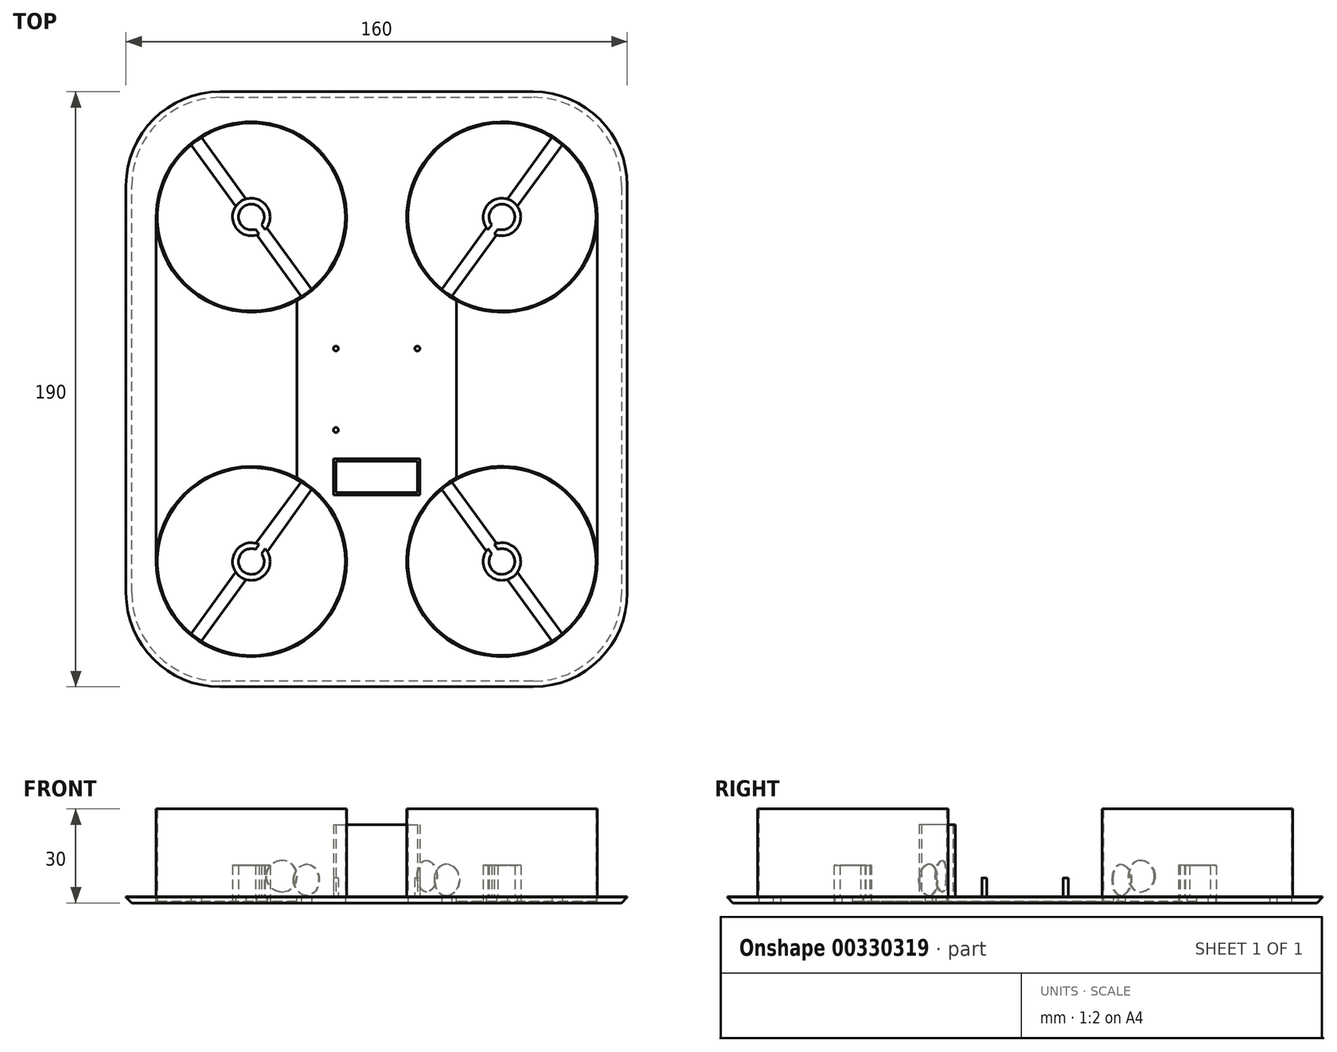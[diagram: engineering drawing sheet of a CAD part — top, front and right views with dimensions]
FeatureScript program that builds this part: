
annotation { "Feature Type Name" : "Feature", "Feature Type Description" : "" }
export const myFeature = defineFeature(function(context is Context, id is Id, definition is map)
    precondition{}
    {
        {
            var Q0;
            Q0=qCreatedBy(makeId("Top.planeOp"),FACE);
            var sketch = newSketch(context, id + "F0", { "sketchPlane" : qUnion([Q0])});
            skLineSegment(sketch, "E0.bottom", {"start": v(-80, 95) * mm, "end": v(80, 95) * mm});
            skLineSegment(sketch, "E0.top", {"start": v(-80, -95) * mm, "end": v(80, -95) * mm});
            skLineSegment(sketch, "E0.left", {"start": v(-80, 95) * mm, "end": v(-80, -95) * mm});
            skLineSegment(sketch, "E0.right", {"start": v(80, 95) * mm, "end": v(80, -95) * mm});
            skArc(sketch, "E1", {"start": v(-20.78, 31.97) * mm, "mid": v(-15.74, 72.65) * mm, "end": v(-55.99, 80.38) * mm});
            skLineSegment(sketch, "E2", {"start": v(-40, 132.2) * mm, "end": v(-40, -105.6) * mm, "construction": true});
            skLineSegment(sketch, "E3", {"start": v(-91.22, 55) * mm, "end": v(115.84, 55) * mm, "construction": true});
            skArc(sketch, "E4", {"start": v(55.99, 80.38) * mm, "mid": v(15.74, 72.65) * mm, "end": v(20.78, 31.97) * mm});
            skLineSegment(sketch, "E5", {"start": v(40, 97.12) * mm, "end": v(40, -118.42) * mm, "construction": true});
            skLineSegment(sketch, "E6", {"start": v(-111.72, -55) * mm, "end": v(120.79, -55) * mm, "construction": true});
            skArc(sketch, "E7", {"start": v(-55.99, -80.38) * mm, "mid": v(-15.74, -72.65) * mm, "end": v(-20.78, -31.97) * mm});
            skArc(sketch, "E8", {"start": v(20.78, -31.97) * mm, "mid": v(15.74, -72.65) * mm, "end": v(55.99, -80.38) * mm});
            skLineSegment(sketch, "E9", {"start": v(99.43, 136.72) * mm, "end": v(-85.41, -117.45) * mm, "construction": true});
            skLineSegment(sketch, "E10", {"start": v(-83.26, 114.48) * mm, "end": v(79.72, -109.61) * mm, "construction": true});
            skLineSegment(sketch, "E11", {"start": v(-55.99, 80.38) * mm, "end": v(-41.7, 60.75) * mm});
            skLineSegment(sketch, "E12", {"start": v(-59.22, 78.03) * mm, "end": v(-44.94, 58.4) * mm});
            skArc(sketch, "E13.trimOffspring", {"start": v(-59.22, 78.03) * mm, "mid": v(-64.26, 37.35) * mm, "end": v(-24.01, 29.62) * mm});
            skLineSegment(sketch, "E14.MirrorCS", {"start": v(55.99, 80.38) * mm, "end": v(41.7, 60.75) * mm});
            skLineSegment(sketch, "E15.MirrorCS", {"start": v(59.22, 78.03) * mm, "end": v(44.94, 58.4) * mm});
            skLineSegment(sketch, "E16.MirrorCS", {"start": v(-59.22, -78.03) * mm, "end": v(-44.94, -58.4) * mm});
            skLineSegment(sketch, "E17.MirrorCS", {"start": v(-55.99, -80.38) * mm, "end": v(-41.7, -60.75) * mm});
            skLineSegment(sketch, "E18.MirrorCS", {"start": v(55.99, -80.38) * mm, "end": v(41.7, -60.75) * mm});
            skLineSegment(sketch, "E19.MirrorCS", {"start": v(59.22, -78.03) * mm, "end": v(44.94, -58.4) * mm});
            skArc(sketch, "E20.trimOffspring", {"start": v(24.01, 29.62) * mm, "mid": v(64.26, 37.35) * mm, "end": v(59.22, 78.03) * mm});
            skArc(sketch, "E21.trimOffspring", {"start": v(59.22, -78.03) * mm, "mid": v(64.26, -37.35) * mm, "end": v(24.01, -29.62) * mm});
            skArc(sketch, "E22.trimOffspring", {"start": v(-24.01, -29.62) * mm, "mid": v(-64.26, -37.35) * mm, "end": v(-59.22, -78.03) * mm});
            skArc(sketch, "E23", {"start": v(-35.06, 51.6) * mm, "mid": v(-35.15, 58.53) * mm, "end": v(-41.7, 60.75) * mm});
            skArc(sketch, "E24", {"start": v(41.7, 60.75) * mm, "mid": v(35.15, 58.53) * mm, "end": v(35.06, 51.6) * mm});
            skArc(sketch, "E25", {"start": v(-38.56, -49.18) * mm, "mid": v(-44.93, -51.58) * mm, "end": v(-44.94, -58.4) * mm});
            skArc(sketch, "E26", {"start": v(44.94, -58.4) * mm, "mid": v(44.85, -51.47) * mm, "end": v(38.3, -49.25) * mm});
            skLineSegment(sketch, "E27.trimOffspring", {"start": v(-35.06, 51.6) * mm, "end": v(-20.78, 31.97) * mm});
            skLineSegment(sketch, "E28.trimOffspring", {"start": v(-38.3, 49.25) * mm, "end": v(-24.01, 29.62) * mm});
            skArc(sketch, "E29.trimOffspring", {"start": v(-44.94, 58.4) * mm, "mid": v(-44.85, 51.47) * mm, "end": v(-38.3, 49.25) * mm});
            skLineSegment(sketch, "E30.trimOffspring", {"start": v(35.06, 51.6) * mm, "end": v(20.78, 31.97) * mm});
            skLineSegment(sketch, "E31.trimOffspring", {"start": v(38.3, 49.25) * mm, "end": v(24.01, 29.62) * mm});
            skArc(sketch, "E32.trimOffspring", {"start": v(38.3, 49.25) * mm, "mid": v(44.85, 51.47) * mm, "end": v(44.94, 58.4) * mm});
            skLineSegment(sketch, "E33.trimOffspring", {"start": v(-34.9, -51.83) * mm, "end": v(-20.78, -31.97) * mm});
            skLineSegment(sketch, "E34.trimOffspring", {"start": v(-38.56, -49.18) * mm, "end": v(-24.01, -29.62) * mm});
            skArc(sketch, "E35.trimOffspring", {"start": v(-41.7, -60.75) * mm, "mid": v(-35.23, -58.64) * mm, "end": v(-34.9, -51.83) * mm});
            skLineSegment(sketch, "E36.trimOffspring", {"start": v(38.3, -49.25) * mm, "end": v(24.01, -29.62) * mm});
            skLineSegment(sketch, "E37.trimOffspring", {"start": v(35.06, -51.6) * mm, "end": v(20.78, -31.97) * mm});
            skArc(sketch, "E38.trimOffspring", {"start": v(35.06, -51.6) * mm, "mid": v(35.15, -58.53) * mm, "end": v(41.7, -60.75) * mm});
            skSolve(sketch);
        }
        {
            var Q0;
            Q0 = qSketchRegion(id + "F0", true);
            extrude(context, id + "F1", {"entities" : qUnion([Q0]), "depth" : 2 * mm});
        }
        {
            var Q0;
            Q0=makeQuery(id+"F1.opExtrude","SWEPT_EDGE",EDGE,{"disambiguationData":[OSD([sQuery(id+"F0.wireOp",EDGE,"E0.bottom"),sQuery(id+"F0.wireOp",EDGE,"E0.left")])]});
            var Q1;
            Q1=makeQuery(id+"F1.opExtrude","SWEPT_EDGE",EDGE,{"disambiguationData":[OSD([sQuery(id+"F0.wireOp",EDGE,"E0.bottom"),sQuery(id+"F0.wireOp",EDGE,"E0.right")])]});
            var Q2;
            Q2=makeQuery(id+"F1.opExtrude","SWEPT_EDGE",EDGE,{"disambiguationData":[OSD([sQuery(id+"F0.wireOp",EDGE,"E0.top"),sQuery(id+"F0.wireOp",EDGE,"E0.right")])]});
            var Q3;
            Q3=makeQuery(id+"F1.opExtrude","SWEPT_EDGE",EDGE,{"disambiguationData":[OSD([sQuery(id+"F0.wireOp",EDGE,"E0.top"),sQuery(id+"F0.wireOp",EDGE,"E0.left")])]});
            fillet(context, id + "F2", {"entities" : qUnion([Q0, Q1, Q2, Q3]), "radius" : 30 * mm, "tangentPropagation" : true, "allowEdgeOverflow" : false});
        }
        {
            var Q0;
            Q0=qCreatedBy(makeId("Top.planeOp"),FACE);
            var sketch = newSketch(context, id + "F3", { "sketchPlane" : qUnion([Q0])});
            skArc(sketch, "E39", {"start": v(-35.57, 50.95) * mm, "mid": v(-43.53, 59.85) * mm, "end": v(-37.51, 49.54) * mm});
            skArc(sketch, "E40", {"start": v(-36.72, 52.54) * mm, "mid": v(-42.41, 58.32) * mm, "end": v(-38.66, 51.12) * mm});
            skLineSegment(sketch, "E41", {"start": v(-48.35, 66.48) * mm, "end": v(-31.44, 43.23) * mm, "construction": true});
            skLineSegment(sketch, "E42", {"start": v(-36.72, 52.54) * mm, "end": v(-35.57, 50.95) * mm});
            skLineSegment(sketch, "E43.MirrorCS", {"start": v(-38.66, 51.12) * mm, "end": v(-37.51, 49.54) * mm});
            skArc(sketch, "E44.MirrorCS", {"start": v(36.72, 52.54) * mm, "mid": v(42.41, 58.32) * mm, "end": v(38.66, 51.12) * mm});
            skArc(sketch, "E45.MirrorCS", {"start": v(35.57, 50.95) * mm, "mid": v(43.53, 59.85) * mm, "end": v(37.51, 49.54) * mm});
            skLineSegment(sketch, "E46.MirrorCS", {"start": v(36.72, 52.54) * mm, "end": v(35.57, 50.95) * mm});
            skLineSegment(sketch, "E47.MirrorCS", {"start": v(38.66, 51.12) * mm, "end": v(37.51, 49.54) * mm});
            skArc(sketch, "E48.MirrorCS", {"start": v(35.57, -50.95) * mm, "mid": v(43.53, -59.85) * mm, "end": v(37.51, -49.54) * mm});
            skArc(sketch, "E49.MirrorCS", {"start": v(36.72, -52.54) * mm, "mid": v(42.41, -58.32) * mm, "end": v(38.66, -51.12) * mm});
            skLineSegment(sketch, "E50.MirrorCS", {"start": v(38.66, -51.12) * mm, "end": v(37.51, -49.54) * mm});
            skLineSegment(sketch, "E51.MirrorCS", {"start": v(36.72, -52.54) * mm, "end": v(35.57, -50.95) * mm});
            skArc(sketch, "E52.MirrorCS", {"start": v(-36.72, -52.54) * mm, "mid": v(-42.41, -58.32) * mm, "end": v(-38.66, -51.12) * mm});
            skLineSegment(sketch, "E53.MirrorCS", {"start": v(-36.72, -52.54) * mm, "end": v(-35.57, -50.95) * mm});
            skLineSegment(sketch, "E54.MirrorCS", {"start": v(-38.66, -51.12) * mm, "end": v(-37.51, -49.54) * mm});
            skArc(sketch, "E55.MirrorCS", {"start": v(-35.57, -50.95) * mm, "mid": v(-43.53, -59.85) * mm, "end": v(-37.51, -49.54) * mm});
            skSolve(sketch);
        }
        {
            var Q0;
            Q0 = qSketchRegion(id + "F3", true);
            extrude(context, id + "F4", {"entities" : qUnion([Q0]), "operationType" : NewBodyOperationType.ADD, "depth" : 12 * mm});
        }
        {
            var Q0;
            Q0=qCreatedBy(makeId("Top.planeOp"),FACE);
            var sketch = newSketch(context, id + "F5", { "sketchPlane" : qUnion([Q0])});
            skCircle(sketch, "E56", {"center": v(-40, 55) * mm, "radius": 30 * mm});
            skCircle(sketch, "E57", {"center": v(-40, 55) * mm, "radius": 30.4 * mm});
            skCircle(sketch, "E58.MirrorC", {"center": v(40, 55) * mm, "radius": 30.4 * mm});
            skCircle(sketch, "E59.MirrorC", {"center": v(40, 55) * mm, "radius": 30 * mm});
            skCircle(sketch, "E60.MirrorC", {"center": v(-40, -55) * mm, "radius": 30.4 * mm});
            skCircle(sketch, "E61.MirrorC", {"center": v(-40, -55) * mm, "radius": 30 * mm});
            skCircle(sketch, "E62.MirrorC", {"center": v(40, -55) * mm, "radius": 30.4 * mm});
            skCircle(sketch, "E63.MirrorC", {"center": v(40, -55) * mm, "radius": 30 * mm});
            skSolve(sketch);
        }
        {
            var Q0;
            Q0 = qSketchRegion(id + "F5", true);
            extrude(context, id + "F6", {"entities" : qUnion([Q0]), "operationType" : NewBodyOperationType.ADD, "depth" : 30 * mm});
        }
        {
            var Q0;
            Q0=qCreatedBy(makeId("Front.planeOp"),FACE);
            var sketch = newSketch(context, id + "F7", { "sketchPlane" : qUnion([Q0])});
            skLineSegment(sketch, "E64", {"start": v(0, 70.13) * mm, "end": v(0, -36.6) * mm, "construction": true});
            skSolve(sketch);
        }
        {
            var Q0;
            Q0=sQuery(id+"F7.wireOp",EDGE,"E64");
            cPlane(context, id + "F8", {"entities" : qUnion([Q0]), "cplaneType" : CPlaneType.LINE_ANGLE, "offset" : 25 * mm, "angle" : 54 * degree, "width" : 150 * mm, "height" : 150 * mm});
        }
        {
            var Q0;
            Q0=qCreatedBy(id+"F8.planeOp",FACE);
            var sketch = newSketch(context, id + "F9", { "sketchPlane" : qUnion([Q0])});
            skCircle(sketch, "E65", {"center": v(0, 7.35) * mm, "radius": 5 * mm});
            skSolve(sketch);
        }
        {
            var Q0;
            Q0=makeQuery(id+"F9.imprint","IMPRINT",FACE,{"disambiguationData":[TD([[makeQuery(id+"F9.imprint","IMPRINT",EDGE,{"derivedFrom":sQuery(id+"F9.wireOp",EDGE,"E65")}),1.0]])]});
            extrude(context, id + "F10", {"entities" : qUnion([Q0]), "operationType" : NewBodyOperationType.REMOVE, "oppositeDirection" : true, "depth" : 60 * mm, "hasSecondDirection" : true, "secondDirectionOppositeDirection" : false, "secondDirectionDepth" : 60 * mm});
        }
        {
            var Q0;
            Q0=sQuery(id+"F7.wireOp",EDGE,"E64");
            cPlane(context, id + "F11", {"entities" : qUnion([Q0]), "cplaneType" : CPlaneType.LINE_ANGLE, "offset" : 25 * mm, "angle" : 126 * degree, "width" : 150 * mm, "height" : 150 * mm});
        }
        {
            var Q0;
            Q0=qCreatedBy(id+"F11.planeOp",FACE);
            var sketch = newSketch(context, id + "F12", { "sketchPlane" : qUnion([Q0])});
            skCircle(sketch, "E66", {"center": v(8.82, 8.55) * mm, "radius": 5 * mm});
            skSolve(sketch);
        }
        {
            var Q0;
            Q0=makeQuery(id+"F12.imprint","IMPRINT",FACE,{"disambiguationData":[TD([[makeQuery(id+"F12.imprint","IMPRINT",EDGE,{"derivedFrom":sQuery(id+"F12.wireOp",EDGE,"E66")}),1.0]])]});
            extrude(context, id + "F13", {"entities" : qUnion([Q0]), "operationType" : NewBodyOperationType.REMOVE, "oppositeDirection" : true, "depth" : 50 * mm, "hasSecondDirection" : true, "secondDirectionOppositeDirection" : false, "secondDirectionDepth" : 50 * mm});
        }
        {
            var Q0;
            Q0=qCreatedBy(makeId("Top.planeOp"),FACE);
            var sketch = newSketch(context, id + "F14", { "sketchPlane" : qUnion([Q0])});
            skCircle(sketch, "E67", {"center": v(-13, 13) * mm, "radius": 0.8 * mm});
            skCircle(sketch, "E68", {"center": v(13, 13) * mm, "radius": 0.8 * mm});
            skCircle(sketch, "E69", {"center": v(-13, -13) * mm, "radius": 0.8 * mm});
            skSolve(sketch);
        }
        {
            var Q0;
            Q0 = qSketchRegion(id + "F14", true);
            extrude(context, id + "F15", {"entities" : qUnion([Q0]), "operationType" : NewBodyOperationType.ADD, "depth" : 8 * mm});
        }
        {
            var Q0;
            Q0=qCreatedBy(makeId("Top.planeOp"),FACE);
            var sketch = newSketch(context, id + "F16", { "sketchPlane" : qUnion([Q0])});
            skLineSegment(sketch, "E70.bottom", {"start": v(-13, -23) * mm, "end": v(13, -23) * mm});
            skLineSegment(sketch, "E70.top", {"start": v(-13, -33) * mm, "end": v(13, -33) * mm});
            skLineSegment(sketch, "E70.left", {"start": v(-13, -23) * mm, "end": v(-13, -33) * mm});
            skLineSegment(sketch, "E70.right", {"start": v(13, -23) * mm, "end": v(13, -33) * mm});
            skLineSegment(sketch, "E71.0", {"start": v(-13.8, -22.2) * mm, "end": v(13.8, -22.2) * mm});
            skLineSegment(sketch, "E71.1", {"start": v(-13.8, -22.2) * mm, "end": v(-13.8, -33.8) * mm});
            skLineSegment(sketch, "E71.2", {"start": v(-13.8, -33.8) * mm, "end": v(13.8, -33.8) * mm});
            skLineSegment(sketch, "E71.3", {"start": v(13.8, -22.2) * mm, "end": v(13.8, -33.8) * mm});
            skSolve(sketch);
        }
        {
            var Q0;
            Q0 = qSketchRegion(id + "F16", true);
            extrude(context, id + "F17", {"entities" : qUnion([Q0]), "operationType" : NewBodyOperationType.ADD, "depth" : 25 * mm});
        }
        {
            var Q0;
            Q0=makeQuery(id+"F1.opExtrude","CAP_EDGE",EDGE,{"disambiguationData":[OSD([sQuery(id+"F0.wireOp",EDGE,"E0.right")])],"isStart":true});
            var Q1;
            {var subQ0=sQuery(id+"F0.wireOp",EDGE,"E0.right");var subQ1=sQuery(id+"F0.wireOp",EDGE,"E0.top");Q1=makeQuery(id+"F2.opFillet","BLEND_EDGE",EDGE,{"blendedFrom":[makeQuery(id+"F1.opExtrude","SWEPT_EDGE",EDGE,{"disambiguationData":[OSD([subQ1,subQ0])]}),makeQuery(id+"F1.opExtrude","CAP_FACE",FACE,{"disambiguationData":[OSD([sQuery(id+"F0.wireOp",EDGE,"E0.bottom"),subQ1,sQuery(id+"F0.wireOp",EDGE,"E0.left"),subQ0,sQuery(id+"F0.wireOp",EDGE,"E1"),sQuery(id+"F0.wireOp",EDGE,"E4"),sQuery(id+"F0.wireOp",EDGE,"E7"),sQuery(id+"F0.wireOp",EDGE,"E8"),sQuery(id+"F0.wireOp",EDGE,"E11"),sQuery(id+"F0.wireOp",EDGE,"E12"),sQuery(id+"F0.wireOp",EDGE,"E13.trimOffspring"),sQuery(id+"F0.wireOp",EDGE,"E14.MirrorCS"),sQuery(id+"F0.wireOp",EDGE,"E15.MirrorCS"),sQuery(id+"F0.wireOp",EDGE,"E16.MirrorCS"),sQuery(id+"F0.wireOp",EDGE,"E17.MirrorCS"),sQuery(id+"F0.wireOp",EDGE,"E18.MirrorCS"),sQuery(id+"F0.wireOp",EDGE,"E19.MirrorCS"),sQuery(id+"F0.wireOp",EDGE,"E20.trimOffspring"),sQuery(id+"F0.wireOp",EDGE,"E21.trimOffspring"),sQuery(id+"F0.wireOp",EDGE,"E22.trimOffspring"),sQuery(id+"F0.wireOp",EDGE,"E23"),sQuery(id+"F0.wireOp",EDGE,"E24"),sQuery(id+"F0.wireOp",EDGE,"E25"),sQuery(id+"F0.wireOp",EDGE,"E26"),sQuery(id+"F0.wireOp",EDGE,"E27.trimOffspring"),sQuery(id+"F0.wireOp",EDGE,"E28.trimOffspring"),sQuery(id+"F0.wireOp",EDGE,"E29.trimOffspring"),sQuery(id+"F0.wireOp",EDGE,"E30.trimOffspring"),sQuery(id+"F0.wireOp",EDGE,"E31.trimOffspring"),sQuery(id+"F0.wireOp",EDGE,"E32.trimOffspring"),sQuery(id+"F0.wireOp",EDGE,"E33.trimOffspring"),sQuery(id+"F0.wireOp",EDGE,"E34.trimOffspring"),sQuery(id+"F0.wireOp",EDGE,"E35.trimOffspring"),sQuery(id+"F0.wireOp",EDGE,"E37.trimOffspring"),sQuery(id+"F0.wireOp",EDGE,"E38.trimOffspring"),sQuery(id+"F0.wireOp",EDGE,"E36.trimOffspring")])],"isStart":true})],"blendedInto":[makeQuery(id+"F1.opExtrude","CAP_FACE",FACE,{"disambiguationData":[OSD([sQuery(id+"F0.wireOp",EDGE,"E0.bottom"),subQ1,sQuery(id+"F0.wireOp",EDGE,"E0.left"),subQ0,sQuery(id+"F0.wireOp",EDGE,"E1"),sQuery(id+"F0.wireOp",EDGE,"E4"),sQuery(id+"F0.wireOp",EDGE,"E7"),sQuery(id+"F0.wireOp",EDGE,"E8"),sQuery(id+"F0.wireOp",EDGE,"E11"),sQuery(id+"F0.wireOp",EDGE,"E12"),sQuery(id+"F0.wireOp",EDGE,"E13.trimOffspring"),sQuery(id+"F0.wireOp",EDGE,"E14.MirrorCS"),sQuery(id+"F0.wireOp",EDGE,"E15.MirrorCS"),sQuery(id+"F0.wireOp",EDGE,"E16.MirrorCS"),sQuery(id+"F0.wireOp",EDGE,"E17.MirrorCS"),sQuery(id+"F0.wireOp",EDGE,"E18.MirrorCS"),sQuery(id+"F0.wireOp",EDGE,"E19.MirrorCS"),sQuery(id+"F0.wireOp",EDGE,"E20.trimOffspring"),sQuery(id+"F0.wireOp",EDGE,"E21.trimOffspring"),sQuery(id+"F0.wireOp",EDGE,"E22.trimOffspring"),sQuery(id+"F0.wireOp",EDGE,"E23"),sQuery(id+"F0.wireOp",EDGE,"E24"),sQuery(id+"F0.wireOp",EDGE,"E25"),sQuery(id+"F0.wireOp",EDGE,"E26"),sQuery(id+"F0.wireOp",EDGE,"E27.trimOffspring"),sQuery(id+"F0.wireOp",EDGE,"E28.trimOffspring"),sQuery(id+"F0.wireOp",EDGE,"E29.trimOffspring"),sQuery(id+"F0.wireOp",EDGE,"E30.trimOffspring"),sQuery(id+"F0.wireOp",EDGE,"E31.trimOffspring"),sQuery(id+"F0.wireOp",EDGE,"E32.trimOffspring"),sQuery(id+"F0.wireOp",EDGE,"E33.trimOffspring"),sQuery(id+"F0.wireOp",EDGE,"E34.trimOffspring"),sQuery(id+"F0.wireOp",EDGE,"E35.trimOffspring"),sQuery(id+"F0.wireOp",EDGE,"E37.trimOffspring"),sQuery(id+"F0.wireOp",EDGE,"E38.trimOffspring"),sQuery(id+"F0.wireOp",EDGE,"E36.trimOffspring")])],"isStart":true})]});}
            var Q2;
            Q2=makeQuery(id+"F1.opExtrude","CAP_EDGE",EDGE,{"disambiguationData":[OSD([sQuery(id+"F0.wireOp",EDGE,"E0.top")])],"isStart":true});
            var Q3;
            {var subQ0=sQuery(id+"F0.wireOp",EDGE,"E0.left");var subQ1=sQuery(id+"F0.wireOp",EDGE,"E0.top");Q3=makeQuery(id+"F2.opFillet","BLEND_EDGE",EDGE,{"blendedFrom":[makeQuery(id+"F1.opExtrude","SWEPT_EDGE",EDGE,{"disambiguationData":[OSD([subQ1,subQ0])]}),makeQuery(id+"F1.opExtrude","CAP_FACE",FACE,{"disambiguationData":[OSD([sQuery(id+"F0.wireOp",EDGE,"E0.bottom"),subQ1,subQ0,sQuery(id+"F0.wireOp",EDGE,"E0.right"),sQuery(id+"F0.wireOp",EDGE,"E1"),sQuery(id+"F0.wireOp",EDGE,"E4"),sQuery(id+"F0.wireOp",EDGE,"E7"),sQuery(id+"F0.wireOp",EDGE,"E8"),sQuery(id+"F0.wireOp",EDGE,"E11"),sQuery(id+"F0.wireOp",EDGE,"E12"),sQuery(id+"F0.wireOp",EDGE,"E13.trimOffspring"),sQuery(id+"F0.wireOp",EDGE,"E14.MirrorCS"),sQuery(id+"F0.wireOp",EDGE,"E15.MirrorCS"),sQuery(id+"F0.wireOp",EDGE,"E16.MirrorCS"),sQuery(id+"F0.wireOp",EDGE,"E17.MirrorCS"),sQuery(id+"F0.wireOp",EDGE,"E18.MirrorCS"),sQuery(id+"F0.wireOp",EDGE,"E19.MirrorCS"),sQuery(id+"F0.wireOp",EDGE,"E20.trimOffspring"),sQuery(id+"F0.wireOp",EDGE,"E21.trimOffspring"),sQuery(id+"F0.wireOp",EDGE,"E22.trimOffspring"),sQuery(id+"F0.wireOp",EDGE,"E23"),sQuery(id+"F0.wireOp",EDGE,"E24"),sQuery(id+"F0.wireOp",EDGE,"E25"),sQuery(id+"F0.wireOp",EDGE,"E26"),sQuery(id+"F0.wireOp",EDGE,"E27.trimOffspring"),sQuery(id+"F0.wireOp",EDGE,"E28.trimOffspring"),sQuery(id+"F0.wireOp",EDGE,"E29.trimOffspring"),sQuery(id+"F0.wireOp",EDGE,"E30.trimOffspring"),sQuery(id+"F0.wireOp",EDGE,"E31.trimOffspring"),sQuery(id+"F0.wireOp",EDGE,"E32.trimOffspring"),sQuery(id+"F0.wireOp",EDGE,"E33.trimOffspring"),sQuery(id+"F0.wireOp",EDGE,"E34.trimOffspring"),sQuery(id+"F0.wireOp",EDGE,"E35.trimOffspring"),sQuery(id+"F0.wireOp",EDGE,"E37.trimOffspring"),sQuery(id+"F0.wireOp",EDGE,"E38.trimOffspring"),sQuery(id+"F0.wireOp",EDGE,"E36.trimOffspring")])],"isStart":true})],"blendedInto":[makeQuery(id+"F1.opExtrude","CAP_FACE",FACE,{"disambiguationData":[OSD([sQuery(id+"F0.wireOp",EDGE,"E0.bottom"),subQ1,subQ0,sQuery(id+"F0.wireOp",EDGE,"E0.right"),sQuery(id+"F0.wireOp",EDGE,"E1"),sQuery(id+"F0.wireOp",EDGE,"E4"),sQuery(id+"F0.wireOp",EDGE,"E7"),sQuery(id+"F0.wireOp",EDGE,"E8"),sQuery(id+"F0.wireOp",EDGE,"E11"),sQuery(id+"F0.wireOp",EDGE,"E12"),sQuery(id+"F0.wireOp",EDGE,"E13.trimOffspring"),sQuery(id+"F0.wireOp",EDGE,"E14.MirrorCS"),sQuery(id+"F0.wireOp",EDGE,"E15.MirrorCS"),sQuery(id+"F0.wireOp",EDGE,"E16.MirrorCS"),sQuery(id+"F0.wireOp",EDGE,"E17.MirrorCS"),sQuery(id+"F0.wireOp",EDGE,"E18.MirrorCS"),sQuery(id+"F0.wireOp",EDGE,"E19.MirrorCS"),sQuery(id+"F0.wireOp",EDGE,"E20.trimOffspring"),sQuery(id+"F0.wireOp",EDGE,"E21.trimOffspring"),sQuery(id+"F0.wireOp",EDGE,"E22.trimOffspring"),sQuery(id+"F0.wireOp",EDGE,"E23"),sQuery(id+"F0.wireOp",EDGE,"E24"),sQuery(id+"F0.wireOp",EDGE,"E25"),sQuery(id+"F0.wireOp",EDGE,"E26"),sQuery(id+"F0.wireOp",EDGE,"E27.trimOffspring"),sQuery(id+"F0.wireOp",EDGE,"E28.trimOffspring"),sQuery(id+"F0.wireOp",EDGE,"E29.trimOffspring"),sQuery(id+"F0.wireOp",EDGE,"E30.trimOffspring"),sQuery(id+"F0.wireOp",EDGE,"E31.trimOffspring"),sQuery(id+"F0.wireOp",EDGE,"E32.trimOffspring"),sQuery(id+"F0.wireOp",EDGE,"E33.trimOffspring"),sQuery(id+"F0.wireOp",EDGE,"E34.trimOffspring"),sQuery(id+"F0.wireOp",EDGE,"E35.trimOffspring"),sQuery(id+"F0.wireOp",EDGE,"E37.trimOffspring"),sQuery(id+"F0.wireOp",EDGE,"E38.trimOffspring"),sQuery(id+"F0.wireOp",EDGE,"E36.trimOffspring")])],"isStart":true})]});}
            var Q4;
            Q4=makeQuery(id+"F1.opExtrude","CAP_EDGE",EDGE,{"disambiguationData":[OSD([sQuery(id+"F0.wireOp",EDGE,"E0.left")])],"isStart":true});
            var Q5;
            {var subQ0=sQuery(id+"F0.wireOp",EDGE,"E0.left");var subQ1=sQuery(id+"F0.wireOp",EDGE,"E0.bottom");Q5=makeQuery(id+"F2.opFillet","BLEND_EDGE",EDGE,{"blendedFrom":[makeQuery(id+"F1.opExtrude","SWEPT_EDGE",EDGE,{"disambiguationData":[OSD([subQ1,subQ0])]}),makeQuery(id+"F1.opExtrude","CAP_FACE",FACE,{"disambiguationData":[OSD([subQ1,sQuery(id+"F0.wireOp",EDGE,"E0.top"),subQ0,sQuery(id+"F0.wireOp",EDGE,"E0.right"),sQuery(id+"F0.wireOp",EDGE,"E1"),sQuery(id+"F0.wireOp",EDGE,"E4"),sQuery(id+"F0.wireOp",EDGE,"E7"),sQuery(id+"F0.wireOp",EDGE,"E8"),sQuery(id+"F0.wireOp",EDGE,"E11"),sQuery(id+"F0.wireOp",EDGE,"E12"),sQuery(id+"F0.wireOp",EDGE,"E13.trimOffspring"),sQuery(id+"F0.wireOp",EDGE,"E14.MirrorCS"),sQuery(id+"F0.wireOp",EDGE,"E15.MirrorCS"),sQuery(id+"F0.wireOp",EDGE,"E16.MirrorCS"),sQuery(id+"F0.wireOp",EDGE,"E17.MirrorCS"),sQuery(id+"F0.wireOp",EDGE,"E18.MirrorCS"),sQuery(id+"F0.wireOp",EDGE,"E19.MirrorCS"),sQuery(id+"F0.wireOp",EDGE,"E20.trimOffspring"),sQuery(id+"F0.wireOp",EDGE,"E21.trimOffspring"),sQuery(id+"F0.wireOp",EDGE,"E22.trimOffspring"),sQuery(id+"F0.wireOp",EDGE,"E23"),sQuery(id+"F0.wireOp",EDGE,"E24"),sQuery(id+"F0.wireOp",EDGE,"E25"),sQuery(id+"F0.wireOp",EDGE,"E26"),sQuery(id+"F0.wireOp",EDGE,"E27.trimOffspring"),sQuery(id+"F0.wireOp",EDGE,"E28.trimOffspring"),sQuery(id+"F0.wireOp",EDGE,"E29.trimOffspring"),sQuery(id+"F0.wireOp",EDGE,"E30.trimOffspring"),sQuery(id+"F0.wireOp",EDGE,"E31.trimOffspring"),sQuery(id+"F0.wireOp",EDGE,"E32.trimOffspring"),sQuery(id+"F0.wireOp",EDGE,"E33.trimOffspring"),sQuery(id+"F0.wireOp",EDGE,"E34.trimOffspring"),sQuery(id+"F0.wireOp",EDGE,"E35.trimOffspring"),sQuery(id+"F0.wireOp",EDGE,"E37.trimOffspring"),sQuery(id+"F0.wireOp",EDGE,"E38.trimOffspring"),sQuery(id+"F0.wireOp",EDGE,"E36.trimOffspring")])],"isStart":true})],"blendedInto":[makeQuery(id+"F1.opExtrude","CAP_FACE",FACE,{"disambiguationData":[OSD([subQ1,sQuery(id+"F0.wireOp",EDGE,"E0.top"),subQ0,sQuery(id+"F0.wireOp",EDGE,"E0.right"),sQuery(id+"F0.wireOp",EDGE,"E1"),sQuery(id+"F0.wireOp",EDGE,"E4"),sQuery(id+"F0.wireOp",EDGE,"E7"),sQuery(id+"F0.wireOp",EDGE,"E8"),sQuery(id+"F0.wireOp",EDGE,"E11"),sQuery(id+"F0.wireOp",EDGE,"E12"),sQuery(id+"F0.wireOp",EDGE,"E13.trimOffspring"),sQuery(id+"F0.wireOp",EDGE,"E14.MirrorCS"),sQuery(id+"F0.wireOp",EDGE,"E15.MirrorCS"),sQuery(id+"F0.wireOp",EDGE,"E16.MirrorCS"),sQuery(id+"F0.wireOp",EDGE,"E17.MirrorCS"),sQuery(id+"F0.wireOp",EDGE,"E18.MirrorCS"),sQuery(id+"F0.wireOp",EDGE,"E19.MirrorCS"),sQuery(id+"F0.wireOp",EDGE,"E20.trimOffspring"),sQuery(id+"F0.wireOp",EDGE,"E21.trimOffspring"),sQuery(id+"F0.wireOp",EDGE,"E22.trimOffspring"),sQuery(id+"F0.wireOp",EDGE,"E23"),sQuery(id+"F0.wireOp",EDGE,"E24"),sQuery(id+"F0.wireOp",EDGE,"E25"),sQuery(id+"F0.wireOp",EDGE,"E26"),sQuery(id+"F0.wireOp",EDGE,"E27.trimOffspring"),sQuery(id+"F0.wireOp",EDGE,"E28.trimOffspring"),sQuery(id+"F0.wireOp",EDGE,"E29.trimOffspring"),sQuery(id+"F0.wireOp",EDGE,"E30.trimOffspring"),sQuery(id+"F0.wireOp",EDGE,"E31.trimOffspring"),sQuery(id+"F0.wireOp",EDGE,"E32.trimOffspring"),sQuery(id+"F0.wireOp",EDGE,"E33.trimOffspring"),sQuery(id+"F0.wireOp",EDGE,"E34.trimOffspring"),sQuery(id+"F0.wireOp",EDGE,"E35.trimOffspring"),sQuery(id+"F0.wireOp",EDGE,"E37.trimOffspring"),sQuery(id+"F0.wireOp",EDGE,"E38.trimOffspring"),sQuery(id+"F0.wireOp",EDGE,"E36.trimOffspring")])],"isStart":true})]});}
            var Q6;
            Q6=makeQuery(id+"F1.opExtrude","CAP_EDGE",EDGE,{"disambiguationData":[OSD([sQuery(id+"F0.wireOp",EDGE,"E0.bottom")])],"isStart":true});
            var Q7;
            {var subQ0=sQuery(id+"F0.wireOp",EDGE,"E0.right");var subQ1=sQuery(id+"F0.wireOp",EDGE,"E0.bottom");Q7=makeQuery(id+"F2.opFillet","BLEND_EDGE",EDGE,{"blendedFrom":[makeQuery(id+"F1.opExtrude","SWEPT_EDGE",EDGE,{"disambiguationData":[OSD([subQ1,subQ0])]}),makeQuery(id+"F1.opExtrude","CAP_FACE",FACE,{"disambiguationData":[OSD([subQ1,sQuery(id+"F0.wireOp",EDGE,"E0.top"),sQuery(id+"F0.wireOp",EDGE,"E0.left"),subQ0,sQuery(id+"F0.wireOp",EDGE,"E1"),sQuery(id+"F0.wireOp",EDGE,"E4"),sQuery(id+"F0.wireOp",EDGE,"E7"),sQuery(id+"F0.wireOp",EDGE,"E8"),sQuery(id+"F0.wireOp",EDGE,"E11"),sQuery(id+"F0.wireOp",EDGE,"E12"),sQuery(id+"F0.wireOp",EDGE,"E13.trimOffspring"),sQuery(id+"F0.wireOp",EDGE,"E14.MirrorCS"),sQuery(id+"F0.wireOp",EDGE,"E15.MirrorCS"),sQuery(id+"F0.wireOp",EDGE,"E16.MirrorCS"),sQuery(id+"F0.wireOp",EDGE,"E17.MirrorCS"),sQuery(id+"F0.wireOp",EDGE,"E18.MirrorCS"),sQuery(id+"F0.wireOp",EDGE,"E19.MirrorCS"),sQuery(id+"F0.wireOp",EDGE,"E20.trimOffspring"),sQuery(id+"F0.wireOp",EDGE,"E21.trimOffspring"),sQuery(id+"F0.wireOp",EDGE,"E22.trimOffspring"),sQuery(id+"F0.wireOp",EDGE,"E23"),sQuery(id+"F0.wireOp",EDGE,"E24"),sQuery(id+"F0.wireOp",EDGE,"E25"),sQuery(id+"F0.wireOp",EDGE,"E26"),sQuery(id+"F0.wireOp",EDGE,"E27.trimOffspring"),sQuery(id+"F0.wireOp",EDGE,"E28.trimOffspring"),sQuery(id+"F0.wireOp",EDGE,"E29.trimOffspring"),sQuery(id+"F0.wireOp",EDGE,"E30.trimOffspring"),sQuery(id+"F0.wireOp",EDGE,"E31.trimOffspring"),sQuery(id+"F0.wireOp",EDGE,"E32.trimOffspring"),sQuery(id+"F0.wireOp",EDGE,"E33.trimOffspring"),sQuery(id+"F0.wireOp",EDGE,"E34.trimOffspring"),sQuery(id+"F0.wireOp",EDGE,"E35.trimOffspring"),sQuery(id+"F0.wireOp",EDGE,"E37.trimOffspring"),sQuery(id+"F0.wireOp",EDGE,"E38.trimOffspring"),sQuery(id+"F0.wireOp",EDGE,"E36.trimOffspring")])],"isStart":true})],"blendedInto":[makeQuery(id+"F1.opExtrude","CAP_FACE",FACE,{"disambiguationData":[OSD([subQ1,sQuery(id+"F0.wireOp",EDGE,"E0.top"),sQuery(id+"F0.wireOp",EDGE,"E0.left"),subQ0,sQuery(id+"F0.wireOp",EDGE,"E1"),sQuery(id+"F0.wireOp",EDGE,"E4"),sQuery(id+"F0.wireOp",EDGE,"E7"),sQuery(id+"F0.wireOp",EDGE,"E8"),sQuery(id+"F0.wireOp",EDGE,"E11"),sQuery(id+"F0.wireOp",EDGE,"E12"),sQuery(id+"F0.wireOp",EDGE,"E13.trimOffspring"),sQuery(id+"F0.wireOp",EDGE,"E14.MirrorCS"),sQuery(id+"F0.wireOp",EDGE,"E15.MirrorCS"),sQuery(id+"F0.wireOp",EDGE,"E16.MirrorCS"),sQuery(id+"F0.wireOp",EDGE,"E17.MirrorCS"),sQuery(id+"F0.wireOp",EDGE,"E18.MirrorCS"),sQuery(id+"F0.wireOp",EDGE,"E19.MirrorCS"),sQuery(id+"F0.wireOp",EDGE,"E20.trimOffspring"),sQuery(id+"F0.wireOp",EDGE,"E21.trimOffspring"),sQuery(id+"F0.wireOp",EDGE,"E22.trimOffspring"),sQuery(id+"F0.wireOp",EDGE,"E23"),sQuery(id+"F0.wireOp",EDGE,"E24"),sQuery(id+"F0.wireOp",EDGE,"E25"),sQuery(id+"F0.wireOp",EDGE,"E26"),sQuery(id+"F0.wireOp",EDGE,"E27.trimOffspring"),sQuery(id+"F0.wireOp",EDGE,"E28.trimOffspring"),sQuery(id+"F0.wireOp",EDGE,"E29.trimOffspring"),sQuery(id+"F0.wireOp",EDGE,"E30.trimOffspring"),sQuery(id+"F0.wireOp",EDGE,"E31.trimOffspring"),sQuery(id+"F0.wireOp",EDGE,"E32.trimOffspring"),sQuery(id+"F0.wireOp",EDGE,"E33.trimOffspring"),sQuery(id+"F0.wireOp",EDGE,"E34.trimOffspring"),sQuery(id+"F0.wireOp",EDGE,"E35.trimOffspring"),sQuery(id+"F0.wireOp",EDGE,"E37.trimOffspring"),sQuery(id+"F0.wireOp",EDGE,"E38.trimOffspring"),sQuery(id+"F0.wireOp",EDGE,"E36.trimOffspring")])],"isStart":true})]});}
            chamfer(context, id + "F18", {"entities" : qUnion([Q0, Q1, Q2, Q3, Q4, Q5, Q6, Q7]), "width" : 1.8 * mm, "tangentPropagation" : true});
        }
        {
            var Q0;
            {var subQ0=sQuery(id+"F0.wireOp",EDGE,"E0.right");var subQ1=sQuery(id+"F0.wireOp",EDGE,"E0.top");var subQ3=sQuery(id+"F0.wireOp",EDGE,"E0.left");var subQ6=sQuery(id+"F0.wireOp",EDGE,"E0.bottom");var subQ7=makeQuery(id+"F1.opExtrude","SWEPT_FACE",FACE,{"disambiguationData":[OSD([subQ6])]});Q0=makeQuery(id+"F17.boolean.opBoolean","SPLIT",FACE,{"disambiguationData":[TD([subQ7])],"derivedFrom":makeQuery(id+"F6.boolean.opBoolean","SPLIT",FACE,{"disambiguationData":[TD([subQ7])],"derivedFrom":makeQuery(id+"F1.opExtrude","CAP_FACE",FACE,{"disambiguationData":[OSD([subQ6,subQ1,subQ3,subQ0,sQuery(id+"F0.wireOp",EDGE,"E1"),sQuery(id+"F0.wireOp",EDGE,"E4"),sQuery(id+"F0.wireOp",EDGE,"E7"),sQuery(id+"F0.wireOp",EDGE,"E8"),sQuery(id+"F0.wireOp",EDGE,"E11"),sQuery(id+"F0.wireOp",EDGE,"E12"),sQuery(id+"F0.wireOp",EDGE,"E13.trimOffspring"),sQuery(id+"F0.wireOp",EDGE,"E14.MirrorCS"),sQuery(id+"F0.wireOp",EDGE,"E15.MirrorCS"),sQuery(id+"F0.wireOp",EDGE,"E16.MirrorCS"),sQuery(id+"F0.wireOp",EDGE,"E17.MirrorCS"),sQuery(id+"F0.wireOp",EDGE,"E18.MirrorCS"),sQuery(id+"F0.wireOp",EDGE,"E19.MirrorCS"),sQuery(id+"F0.wireOp",EDGE,"E20.trimOffspring"),sQuery(id+"F0.wireOp",EDGE,"E21.trimOffspring"),sQuery(id+"F0.wireOp",EDGE,"E22.trimOffspring"),sQuery(id+"F0.wireOp",EDGE,"E23"),sQuery(id+"F0.wireOp",EDGE,"E24"),sQuery(id+"F0.wireOp",EDGE,"E25"),sQuery(id+"F0.wireOp",EDGE,"E26"),sQuery(id+"F0.wireOp",EDGE,"E27.trimOffspring"),sQuery(id+"F0.wireOp",EDGE,"E28.trimOffspring"),sQuery(id+"F0.wireOp",EDGE,"E29.trimOffspring"),sQuery(id+"F0.wireOp",EDGE,"E30.trimOffspring"),sQuery(id+"F0.wireOp",EDGE,"E31.trimOffspring"),sQuery(id+"F0.wireOp",EDGE,"E32.trimOffspring"),sQuery(id+"F0.wireOp",EDGE,"E33.trimOffspring"),sQuery(id+"F0.wireOp",EDGE,"E34.trimOffspring"),sQuery(id+"F0.wireOp",EDGE,"E35.trimOffspring"),sQuery(id+"F0.wireOp",EDGE,"E37.trimOffspring"),sQuery(id+"F0.wireOp",EDGE,"E38.trimOffspring"),sQuery(id+"F0.wireOp",EDGE,"E36.trimOffspring")])],"isStart":false})})});}
            var sketch = newSketch(context, id + "F19", { "sketchPlane" : qUnion([Q0])});
            skLineSegment(sketch, "E72", {"start": v(-70.4, 54.86) * mm, "end": v(-70.4, -55) * mm});
            skLineSegment(sketch, "E73", {"start": v(-25.44, -28.32) * mm, "end": v(-25.44, 28.32) * mm});
            skArc(sketch, "E74.0", {"start": v(-70.4, 54.86) * mm, "mid": v(-55.46, 28.82) * mm, "end": v(-25.44, 28.32) * mm});
            skArc(sketch, "E75.0", {"start": v(-25.44, -28.32) * mm, "mid": v(-55.51, -28.86) * mm, "end": v(-70.4, -55) * mm});
            skLineSegment(sketch, "E76.MirrorCS", {"start": v(25.44, -28.32) * mm, "end": v(25.44, 28.32) * mm});
            skArc(sketch, "E77.MirrorCS", {"start": v(70.4, 54.86) * mm, "mid": v(55.46, 28.82) * mm, "end": v(25.44, 28.32) * mm});
            skArc(sketch, "E78.MirrorCS", {"start": v(25.44, -28.32) * mm, "mid": v(55.51, -28.86) * mm, "end": v(70.4, -55) * mm});
            skLineSegment(sketch, "E79.MirrorCS", {"start": v(70.4, 54.86) * mm, "end": v(70.4, -55) * mm});
            skSolve(sketch);
        }
        {
            var Q0;
            Q0 = qSketchRegion(id + "F19", true);
            extrude(context, id + "F20", {"entities" : qUnion([Q0]), "operationType" : NewBodyOperationType.REMOVE, "oppositeDirection" : true, "depth" : 1.6 * mm});
        }
    });
